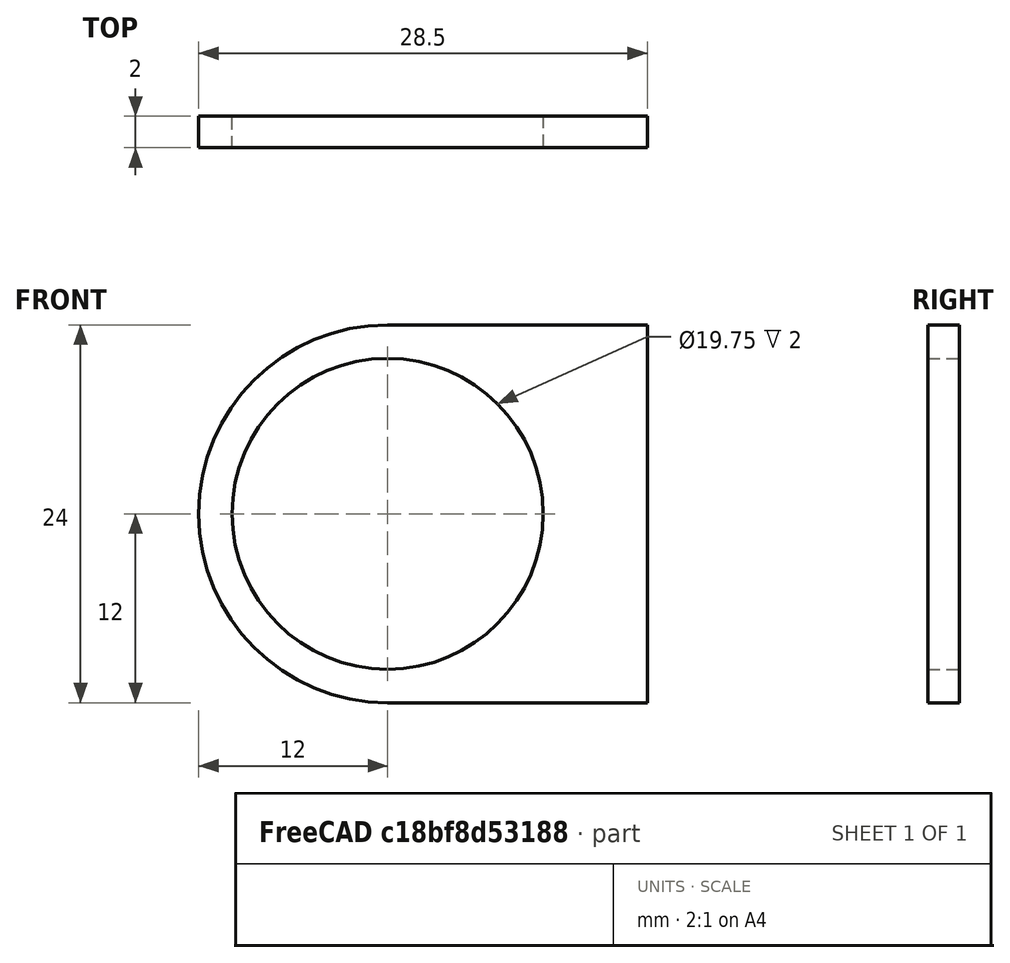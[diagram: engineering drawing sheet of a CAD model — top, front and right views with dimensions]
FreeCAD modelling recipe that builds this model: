
FCSTD DOCUMENT  (FreeCAD 1.0R)
Label: CW-Pad-Side
License: All rights reserved
LicenseURL: https://en.wikipedia.org/wiki/All_rights_reserved
objects: Sketcher::SketchObject×1, PartDesign::Pad×1, PartDesign::Body×1, Part::Part2DObjectPython×1
note: 7 computed .brp shape members not serialized (recipe doc carries the construction recipe); baked Part::Feature solids carry a one-line shape summary decoded from their .brp

FEATURE [Sketcher::SketchObject] Sketch
  ArcFitTolerance = 1e-06
  AttachmentSupport = -> [XZ_Plane]
  FullyConstrained = true
  MakeInternals = false
  MapMode = 5
  Placement = pos=(0,0,0) rot=(1,0,0;1.5708rad)
  sketch-geometry (9):
    g0: GeomPoint [constr] X=0 Y=0 Z=0
    g1: GeomPoint [constr] X=0 Y=0 Z=0
    g2: LineSegment StartX=-15 StartY=-12 StartZ=0 EndX=1.5 EndY=-12 EndZ=0
    g3: ArcOfCircle CenterX=-15 CenterY=8.3e-14 CenterZ=0 NormalX=0 NormalY=0 NormalZ=1 AngleXU=0 Radius=12 StartAngle=1.5708 EndAngle=4.71239
    g4: LineSegment StartX=1.5 StartY=12 StartZ=0 EndX=1.5 EndY=-12 EndZ=0
    g5: LineSegment StartX=1.5 StartY=12 StartZ=0 EndX=-15 EndY=12 EndZ=0
    g6: Circle [constr] CenterX=-15 CenterY=8.3e-14 CenterZ=0 NormalX=0 NormalY=0 NormalZ=1 AngleXU=0 Radius=9.875
    g7: LineSegment [constr] StartX=1.5 StartY=30 StartZ=0 EndX=1.5 EndY=-30 EndZ=0
    g8: Circle CenterX=-15 CenterY=8.3e-14 CenterZ=0 NormalX=0 NormalY=0 NormalZ=1 AngleXU=0 Radius=9.875
  constraints (21):
    c: Coincident(g0,g-1)
    c: Coincident(g1,g0)
    c: Horizontal(g2)
    c: Distance(g2,g5) = 24
    c: Coincident(g3,g2)
    c: Coincident(g3,g5)
    c: DistanceX(g3,g0) = 15
    c: Vertical(g4)
    c: DistanceX(g0,g4) = 1.5
    c: Coincident(g5,g4)
    c: Parallel(g5,g2)
    c: Diameter(g6) = 19.75
    c: Coincident(g6,g3)
    c: DistanceY(g7,g7) = 60
    c: DistanceX(g0,g7) = 1.5
    c: Symmetric(g7,g7,g-1)
    c: Symmetric(g3,g2,g-1)
    c: Vertical(g3,g3)
    c: Coincident(g2,g4)
    c: Diameter(g8) = 19.75
    c: Coincident(g8,g3)
FEATURE [PartDesign::Pad] Pad
  Direction = (0,-1,2e-16)
  Length = 2
  Length2 = 10
  Midplane = true
  Placement = pos=(0,0,0) rot=(1,0,0;1.5708rad)
  Profile = -> Sketch
  ReferenceAxis = -> Sketch [N_Axis]
  Refine = true
  Suppressed = false
  Type = 0
FEATURE [PartDesign::Body] Body  label="CW-Pad-Side"
  AllowCompound = false
  Group = -> [Sketch,Pad]
  Origin = -> Origin
  Tip = -> Pad
FEATURE [Part::Part2DObjectPython] Shape2DView  # Draft 2D object (typed FeaturePython)
  AutoUpdate = true
  Base = -> Pad
  Clip = false
  FuseArch = false
  HiddenLines = false
  InPlace = true
  OnlySolids = false
  Projection = (0,-1,0)
  ProjectionMode = 0
  SegmentLength = 0.05
  Tessellation = false
  VisibleOnly = false
